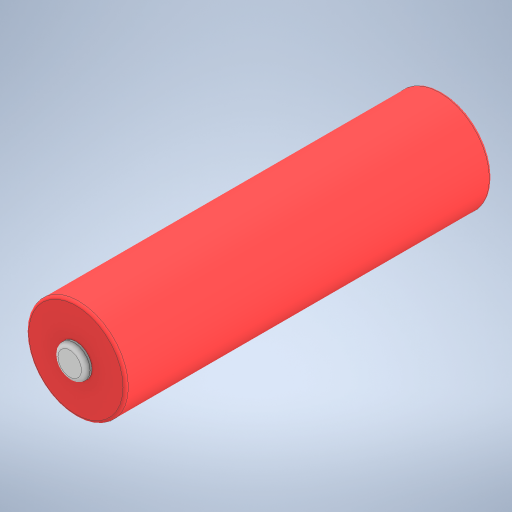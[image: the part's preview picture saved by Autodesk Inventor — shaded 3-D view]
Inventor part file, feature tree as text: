
AUTODESK INVENTOR PART (.ipt)
format: ipt  version: 2023.1 (Build 271208000, 208)  size: 256,512 bytes
history: native  units: mm
features: extrude x2, fillet x2, sketch x2, other x1
ambient origin geometry x8: Origin, YZ Plane, XZ Plane, XY Plane, X Axis, Y Axis, Z Axis, Center Point
bodies: Body1 (feature_tree)
feature tree (7):
  other  "솔리드1"
  extrude  "돌출1"  Depth=18.6mm
  fillet  "모깎기1"  Radius=68.4mm
  extrude  "돌출3"  Depth=0.5mm
  fillet  "모깎기3"  Radius=6.0mm
  sketch  "스케치1"
  sketch  "스케치4"
